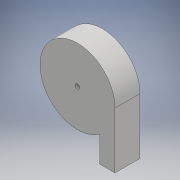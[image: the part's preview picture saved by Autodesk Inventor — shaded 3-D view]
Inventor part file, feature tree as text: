
AUTODESK INVENTOR PART (.ipt)
format: ipt  version: 2017 (Build 210142000, 142)  size: 135,168 bytes
history: native  units: mm
features: sketch x5, extrude x4, shell x1, hole x1
ambient origin geometry x8: Origin, YZ Plane, XZ Plane, XY Plane, X Axis, Y Axis, Z Axis, Center Point
bodies: Solid1 (feature_tree)
feature tree (11):
  extrude  "Extrusion1"  Depth=60.0mm
  shell  "Shell1"  Thickness=45.0mm
  extrude  "Extrusion9"  Depth=20.0mm TaperAngle=0.0deg
  extrude  "Extrusion10"  Depth=3.0mm
  extrude  "Extrusion11"  Depth=3.0mm TaperAngle=0.0deg
  hole  "Hole3"  [1 undecoded]
  sketch  "Sketch1"  dims[d0=50.0mm d1=60.0mm d4=45.0mm]
  sketch  "Sketch11"  dims[d5=12.0mm d6=20.0mm d7=0.0mm]
  sketch  "Sketch12"  dims[d11=3.0mm d44=60.0mm]
  sketch  "Sketch13"  dims[d45=5.0mm d46=0.0mm d47=3.0mm d48=0.0mm]
  sketch  "Sketch14"  dims[d49=3.5mm d50=3.5mm d51=6.0mm d52=4.0mm d53=2.0mm d54=90.0deg d55=3.0mm d56=0.0mm d57=54.0mm d58=14.0mm d59=0.0mm d24=1.0mm d25=1.0mm]
note: 1 required parameter value undecoded (feature->parameter linkage not recoverable at this tier; creation-order binding heuristic only, values carry confidence <= 0.55)
